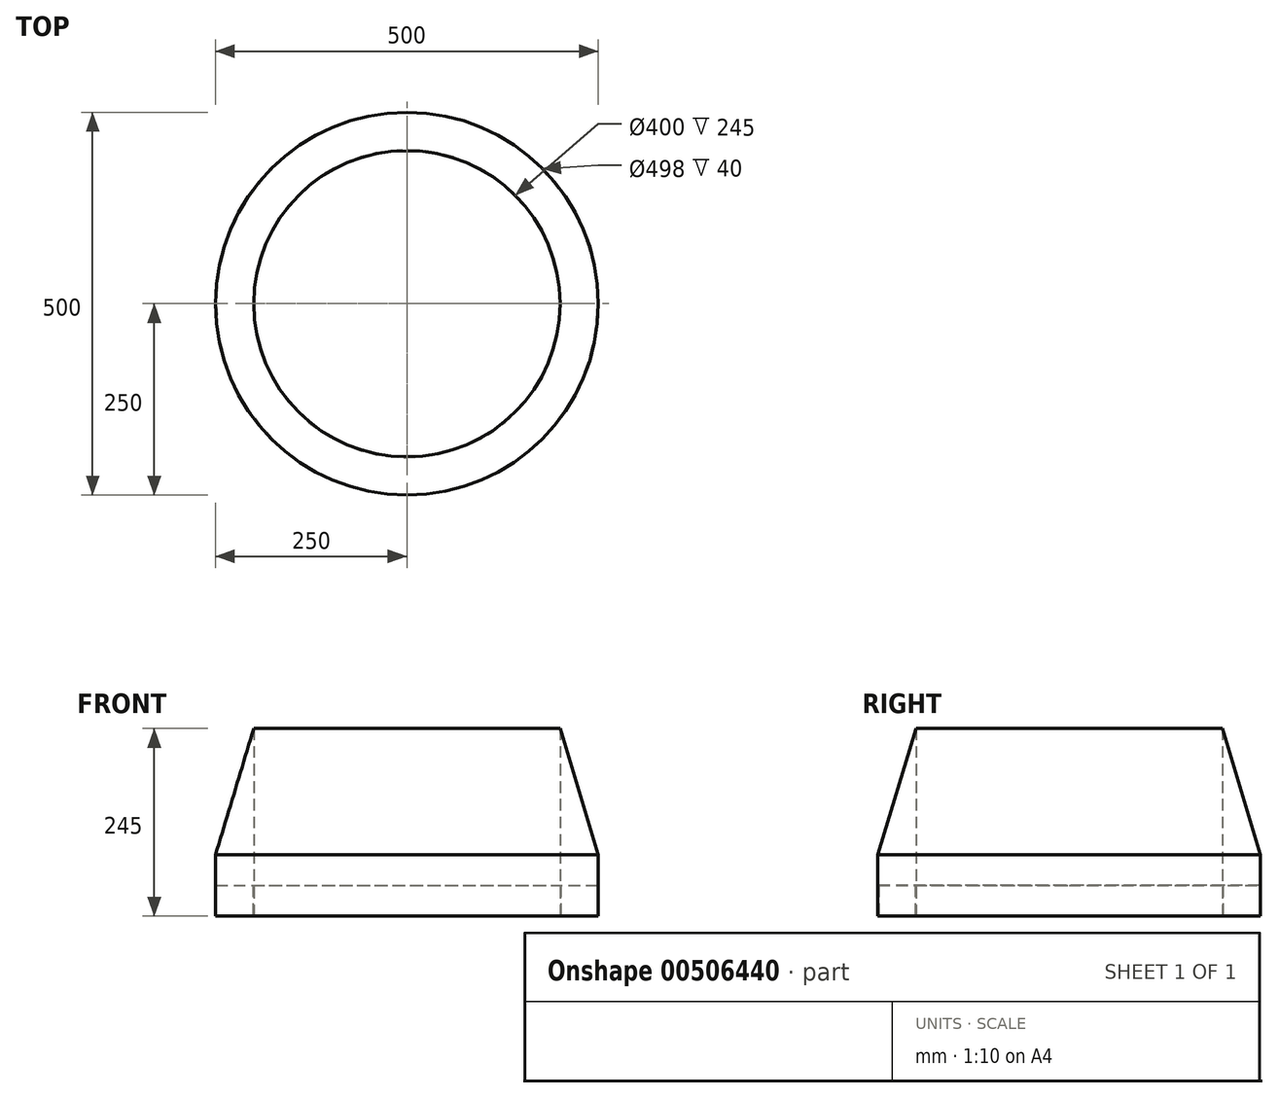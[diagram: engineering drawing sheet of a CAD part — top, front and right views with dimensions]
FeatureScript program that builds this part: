
annotation { "Feature Type Name" : "Feature", "Feature Type Description" : "" }
export const myFeature = defineFeature(function(context is Context, id is Id, definition is map)
    precondition{}
    {
        {
            var Q0;
            Q0=qCreatedBy(makeId("Front.planeOp"),FACE);
            var sketch = newSketch(context, id + "F0", { "sketchPlane" : qUnion([Q0])});
            skLineSegment(sketch, "E0", {"start": v(0, -139.25) * mm, "end": v(0, 240.83) * mm, "construction": true});
            skLineSegment(sketch, "E1", {"start": v(-200, -67.22) * mm, "end": v(-200, 177.78) * mm});
            skLineSegment(sketch, "E2", {"start": v(-200, 177.78) * mm, "end": v(-250, 12.78) * mm});
            skLineSegment(sketch, "E3", {"start": v(-250, 12.78) * mm, "end": v(-250, -67.22) * mm});
            skLineSegment(sketch, "E4", {"start": v(-250, -67.22) * mm, "end": v(-249, -67.22) * mm});
            skLineSegment(sketch, "E5", {"start": v(-249, -67.22) * mm, "end": v(-249, -27.22) * mm});
            skLineSegment(sketch, "E6", {"start": v(-249, -27.22) * mm, "end": v(-201, -27.22) * mm});
            skLineSegment(sketch, "E7", {"start": v(-201, -27.22) * mm, "end": v(-201, -67.22) * mm});
            skLineSegment(sketch, "E8", {"start": v(-201, -67.22) * mm, "end": v(-200, -67.22) * mm});
            skSolve(sketch);
        }
        {
            var Q0;
            Q0=qSketchRegion(id+"F0",true);
            var Q1;
            Q1=sQuery(id+"F0.wireOp",EDGE,"E0");
            revolve(context, id + "F1", {"entities" : qUnion([Q0]), "axis" : qUnion([Q1]), "revolveType" : RevolveType.FULL});
        }
    });
